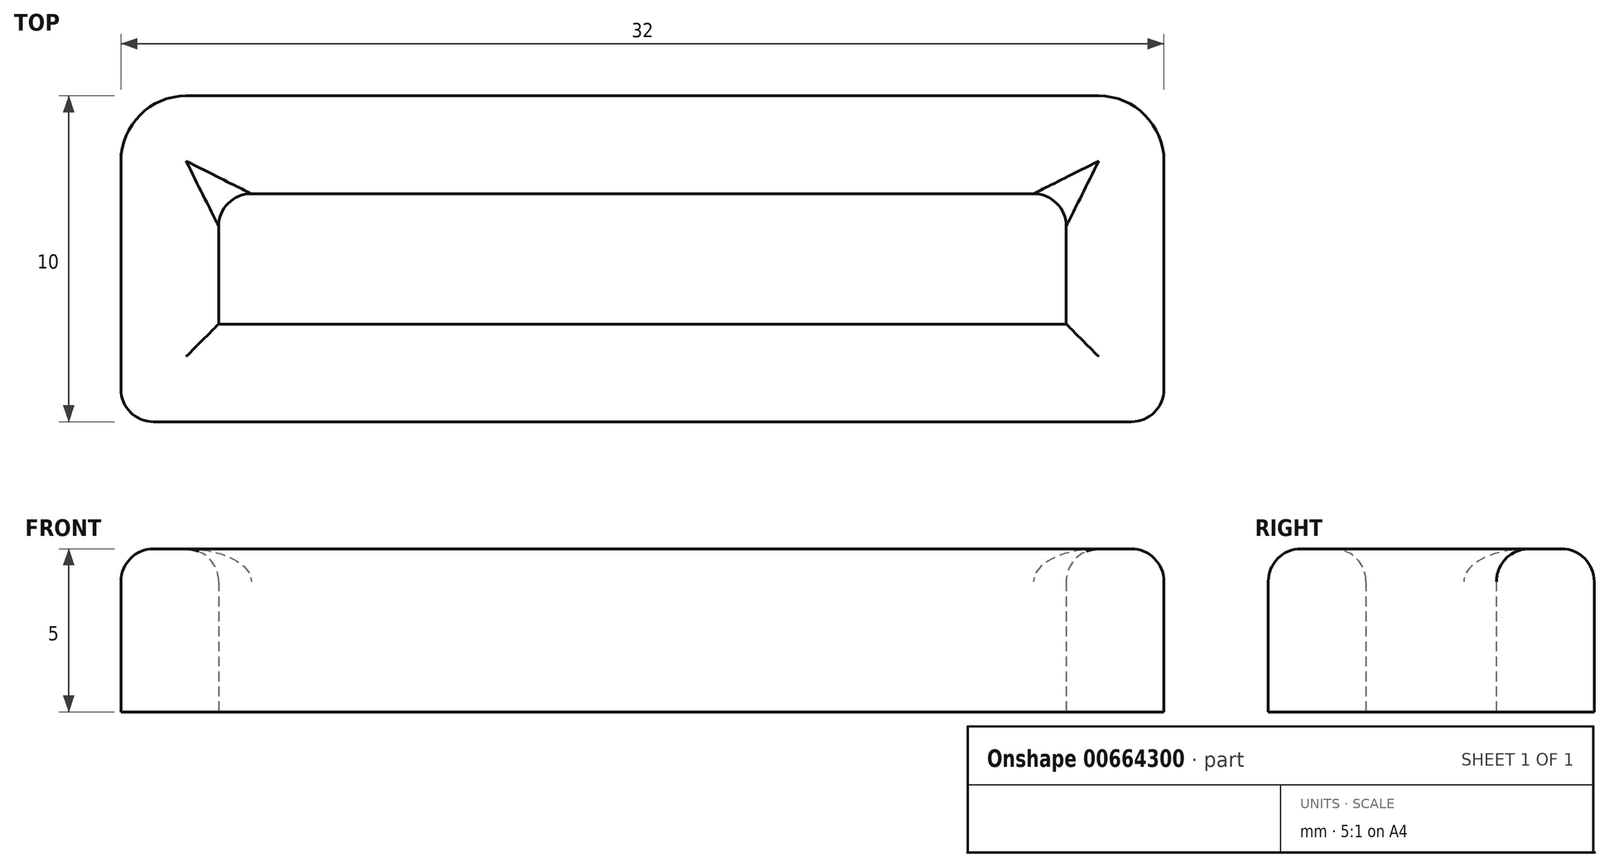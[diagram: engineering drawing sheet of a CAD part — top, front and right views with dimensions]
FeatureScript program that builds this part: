
annotation { "Feature Type Name" : "Feature", "Feature Type Description" : "" }
export const myFeature = defineFeature(function(context is Context, id is Id, definition is map)
    precondition{}
    {
        {
            var Q0;
            Q0=qCreatedBy(makeId("Top.planeOp"),FACE);
            var sketch = newSketch(context, id + "F0", { "sketchPlane" : qUnion([Q0])});
            skLineSegment(sketch, "E0.bottom", {"start": v(16, -5) * mm, "end": v(-16, -5) * mm});
            skLineSegment(sketch, "E0.top", {"start": v(16, 5) * mm, "end": v(-16, 5) * mm});
            skLineSegment(sketch, "E0.left", {"start": v(16, -5) * mm, "end": v(16, 5) * mm});
            skLineSegment(sketch, "E0.right", {"start": v(-16, -5) * mm, "end": v(-16, 5) * mm});
            skPoint(sketch, "E0.middle", {"position": v(0, 0) * mm});
            skSolve(sketch);
        }
        {
            var Q0;
            Q0=makeQuery(id+"F0.imprint","IMPRINT",FACE,{"disambiguationData":[TD([[makeQuery(id+"F0.imprint","IMPRINT",EDGE,{"derivedFrom":sQuery(id+"F0.wireOp",EDGE,"E0.bottom")}),-1.0]])]});
            extrude(context, id + "F1", {"entities" : qUnion([Q0]), "depth" : 5 * mm, "offsetDistance" : 25 * mm});
        }
        {
            var Q0;
            Q0=makeQuery(id+"F1.opExtrude","CAP_FACE",FACE,{"disambiguationData":[OSD([sQuery(id+"F0.wireOp",EDGE,"E0.bottom"),sQuery(id+"F0.wireOp",EDGE,"E0.top"),sQuery(id+"F0.wireOp",EDGE,"E0.left"),sQuery(id+"F0.wireOp",EDGE,"E0.right")])],"isStart":false});
            var Q1;
            Q1=makeQuery(id+"F1.opExtrude","CAP_FACE",FACE,{"disambiguationData":[OSD([sQuery(id+"F0.wireOp",EDGE,"E0.bottom"),sQuery(id+"F0.wireOp",EDGE,"E0.top"),sQuery(id+"F0.wireOp",EDGE,"E0.left"),sQuery(id+"F0.wireOp",EDGE,"E0.right")])],"isStart":true});
            shell(context, id + "F2", {"entities" : qUnion([Q0, Q1]), "thickness" : 3 * mm});
        }
        {
            var Q0;
            Q0=makeQuery(id+"F1.opExtrude","CAP_FACE",FACE,{"disambiguationData":[OSD([sQuery(id+"F0.wireOp",EDGE,"E0.bottom"),sQuery(id+"F0.wireOp",EDGE,"E0.top"),sQuery(id+"F0.wireOp",EDGE,"E0.left"),sQuery(id+"F0.wireOp",EDGE,"E0.right")])],"isStart":false});
            fillet(context, id + "F3", {"entities" : qUnion([Q0]), "radius" : 1 * mm, "tangentPropagation" : true, "allowEdgeOverflow" : false});
        }
        {
            var Q0;
            Q0=makeQuery(id+"F1.opExtrude","SWEPT_EDGE",EDGE,{"disambiguationData":[OSD([sQuery(id+"F0.wireOp",EDGE,"E0.top"),sQuery(id+"F0.wireOp",EDGE,"E0.right")])]});
            var Q1;
            Q1=makeQuery(id+"F1.opExtrude","SWEPT_EDGE",EDGE,{"disambiguationData":[OSD([sQuery(id+"F0.wireOp",EDGE,"E0.top"),sQuery(id+"F0.wireOp",EDGE,"E0.left")])]});
            fillet(context, id + "F4", {"entities" : qUnion([Q0, Q1]), "radius" : 2 * mm, "tangentPropagation" : true, "allowEdgeOverflow" : false});
        }
        {
            var Q0;
            {var subQ0=sQuery(id+"F0.wireOp",EDGE,"E0.right");var subQ1=sQuery(id+"F0.wireOp",EDGE,"E0.top");Q0=makeQuery(id+"F3.opFillet","BLEND_EDGE",EDGE,{"blendedFrom":[makeQuery(id+"F2.opShell","OFFSET_EDGE",EDGE,{"disambiguationData":[OSD([subQ1]),TDD([makeQuery(id+"F1.opExtrude","CAP_EDGE",EDGE,{"disambiguationData":[OSD([subQ1])],"isStart":false})])]}),makeQuery(id+"F2.opShell","OFFSET_EDGE",EDGE,{"disambiguationData":[OSD([subQ0]),TDD([makeQuery(id+"F1.opExtrude","CAP_EDGE",EDGE,{"disambiguationData":[OSD([subQ0])],"isStart":false})])]})],"blendedInto":[]});}
            var Q1;
            {var subQ0=sQuery(id+"F0.wireOp",EDGE,"E0.left");var subQ1=sQuery(id+"F0.wireOp",EDGE,"E0.top");Q1=makeQuery(id+"F3.opFillet","BLEND_EDGE",EDGE,{"blendedFrom":[makeQuery(id+"F2.opShell","OFFSET_EDGE",EDGE,{"disambiguationData":[OSD([subQ1]),TDD([makeQuery(id+"F1.opExtrude","CAP_EDGE",EDGE,{"disambiguationData":[OSD([subQ1])],"isStart":false})])]}),makeQuery(id+"F2.opShell","OFFSET_EDGE",EDGE,{"disambiguationData":[OSD([subQ0]),TDD([makeQuery(id+"F1.opExtrude","CAP_EDGE",EDGE,{"disambiguationData":[OSD([subQ0])],"isStart":false})])]})],"blendedInto":[]});}
            fillet(context, id + "F5", {"entities" : qUnion([Q0, Q1]), "radius" : 1 * mm, "tangentPropagation" : true, "allowEdgeOverflow" : false});
        }
        {
            var Q0;
            Q0=makeQuery(id+"F1.opExtrude","SWEPT_EDGE",EDGE,{"disambiguationData":[OSD([sQuery(id+"F0.wireOp",EDGE,"E0.bottom"),sQuery(id+"F0.wireOp",EDGE,"E0.right")])]});
            var Q1;
            Q1=makeQuery(id+"F1.opExtrude","SWEPT_EDGE",EDGE,{"disambiguationData":[OSD([sQuery(id+"F0.wireOp",EDGE,"E0.bottom"),sQuery(id+"F0.wireOp",EDGE,"E0.left")])]});
            fillet(context, id + "F6", {"entities" : qUnion([Q0, Q1]), "radius" : 1 * mm, "tangentPropagation" : true, "allowEdgeOverflow" : false});
        }
    });
